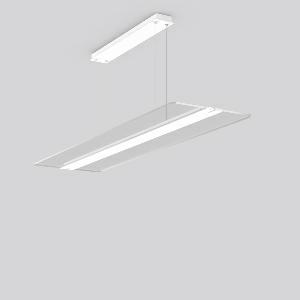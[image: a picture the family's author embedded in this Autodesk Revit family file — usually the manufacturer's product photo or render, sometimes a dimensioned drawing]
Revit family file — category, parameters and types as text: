
# Revit family: twindot_s_312263_002_1_3b57
name_source: partatom
category: Lighting Fixtures
units: mm (PartAtom-declared; Revit-internal decimal feet)

## family parameters
Cut with Voids When Loaded = No
Host = Face
Light Source = No
Part Type = Normal
Room Calculation Point = No
Round Connector Dimension = Use Diameter
Shared = No

## types (1)
- TWINDOT S (1 x LED Modul 840, 6500 lm, 4000)
    Apparent Load = 54 VA
    CIE Flux Codes = 47 77 94 55 100
    Color Rendering = 80
    Color Temperature = 4000
    Default Elevation = 1800 mm
    Description = Series: TWINDOT S
LED pendant luminaire with extremely flat and frameless appearance. Middle bar made of aluminium extrusion profile, powder-coated. Transparent light guide made of UV-resistant acrylic glass (PMMA) with TWINDOT prismatic. Light control with perfectly glare-free TWINDOT technology for pleasantly gentle light with soft shadows. Even and wide indirect and direct light distribution. Direct 55%, indirect 45% light emission. 4-point steel cable suspension, steplessly adjustable. Converter integrated in the canopy (powder-coated white). Power supply through suspension cable. 
Colour: traffic white, matt (RAL 9016)
Length: 1200 mm
Width: 350 mm
Height: 20 mm
Suspension length: 500-1200 mm
Lamp: LED
Socket: without socket
Colour temperature: 4000K
Colour rendering index (CRI): 80
System power: 54 W
Rated luminous flux: 6500 lm
Luminous efficiency: 120 lm/W
Control gear: Regulated power supply
Protection class: I
Type of protection: IP 20
    Height = 20 mm  [stored 0.0656168 ft]
    Lamp = 1 x LED Modul 840
    Lamp Light Flux = 6500 lm
    Lamp count = 1
    Length = 1200 mm
    Lifetime = 50000 h
    Luminous efficacy = 120 lm/W
    Manufacturer = RZB
    ModVariant = No
    Model = 312263.002.1
    Mounting Place = Ceiling
    Mounting Type = Pendant
    Number of Poles = 1
    OnlyDefault = Yes
    Power Factor = 1
    Product Name = TWINDOT S
    Product group = Pendant modular luminaires
    ProductGroupID = 906
    Protection Class = Protection class I
    Protection Degree = IP 20
    RLX_Detail_Level = 1
    RLX_Emergency_Light_Flux = 0 lm
    RLX_Emergency_Type = 0
    RLX_Emergency_Type_DB = No
    RlxData = <blob elided: 35373 chars, md5=17c488ef>
    Socket = socket
    Standby Power = 0 W
    System Light Flux = 6500 lm
    System Power = 54 W
    Type Comments = Product without accessories
    Type Image = 312263.002.jpg
    URL = http://relux.com
    VarID = ---
    Voltage = 230 V
    Voltage Range = 220-240 V
    Weight = 0.00 kg
    Width = 350 mm

note: [stored X ft] marks values corroborated as IEEE doubles in the binary element streams (Revit-internal decimal feet)

## geometry (parser evidence)
native form markers: Blend x4, Sweep x13
no freeform markers — native parametric forms only
